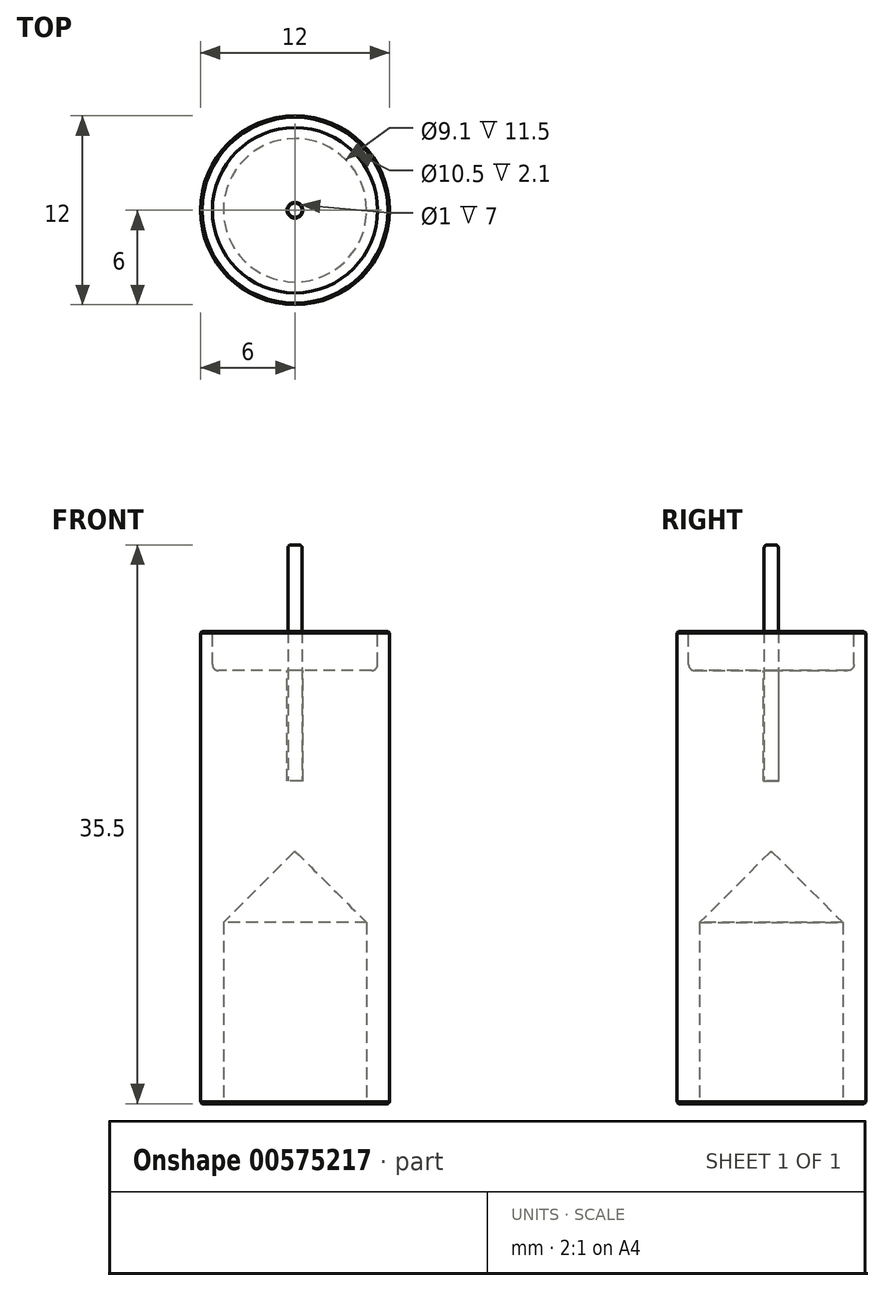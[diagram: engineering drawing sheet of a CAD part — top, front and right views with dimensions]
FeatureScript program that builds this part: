
annotation { "Feature Type Name" : "Feature", "Feature Type Description" : "" }
export const myFeature = defineFeature(function(context is Context, id is Id, definition is map)
    precondition{}
    {
        {
            var Q0;
            Q0=qCreatedBy(makeId("Top.planeOp"),FACE);
            var sketch = newSketch(context, id + "F0", { "sketchPlane" : qUnion([Q0])});
            skCircle(sketch, "E0", {"center": v(0, 0) * mm, "radius": 6 * mm});
            skSolve(sketch);
        }
        {
            var Q0;
            Q0 = qSketchRegion(id + "F0", true);
            extrude(context, id + "F1", {"entities" : qUnion([Q0]), "depth" : 30 * mm, "offsetDistance" : 25 * mm});
        }
        {
            var Q0;
            Q0=qCreatedBy(makeId("Top.planeOp"),FACE);
            var sketch = newSketch(context, id + "F2", { "sketchPlane" : qUnion([Q0])});
            skCircle(sketch, "E1", {"center": v(0, 0) * mm, "radius": 4.55 * mm});
            skSolve(sketch);
        }
        {
            var Q0;
            Q0 = qSketchRegion(id + "F2", true);
            extrude(context, id + "F3", {"entities" : qUnion([Q0]), "operationType" : NewBodyOperationType.REMOVE, "depth" : 16 * mm, "offsetDistance" : 25 * mm});
        }
        {
            var Q0;
            Q0=makeQuery(id+"F3.boolean.opBoolean","COPY",FACE,{"derivedFrom":makeQuery(id+"F3.opExtrude","CAP_FACE",FACE,{"disambiguationData":[OSD([sQuery(id+"F2.wireOp",EDGE,"E1")])],"isStart":false})});
            chamfer(context, id + "F4", {"entities" : qUnion([Q0]), "width" : 4.5 * mm, "tangentPropagation" : true});
        }
        {
            var Q0;
            Q0=makeQuery(id+"F1.opExtrude","CAP_FACE",FACE,{"disambiguationData":[OSD([sQuery(id+"F0.wireOp",EDGE,"E0")])],"isStart":false});
            var sketch = newSketch(context, id + "F5", { "sketchPlane" : qUnion([Q0])});
            skCircle(sketch, "E2", {"center": v(0, 0) * mm, "radius": 5.25 * mm});
            skSolve(sketch);
        }
        {
            var Q0;
            Q0 = qSketchRegion(id + "F5", true);
            extrude(context, id + "F6", {"entities" : qUnion([Q0]), "operationType" : NewBodyOperationType.REMOVE, "oppositeDirection" : true, "depth" : 2.5 * mm, "offsetDistance" : 25 * mm});
        }
        {
            var Q0;
            Q0=makeQuery(id+"F6.boolean.opBoolean","COPY",FACE,{"derivedFrom":makeQuery(id+"F6.opExtrude","CAP_FACE",FACE,{"disambiguationData":[OSD([sQuery(id+"F5.wireOp",EDGE,"E2")])],"isStart":false})});
            var sketch = newSketch(context, id + "F7", { "sketchPlane" : qUnion([Q0])});
            skCircle(sketch, "E3", {"center": v(0, 0) * mm, "radius": 0.5 * mm});
            skSolve(sketch);
        }
        {
            var Q0;
            Q0 = qSketchRegion(id + "F7", true);
            extrude(context, id + "F8", {"entities" : qUnion([Q0]), "operationType" : NewBodyOperationType.REMOVE, "oppositeDirection" : true, "depth" : 7 * mm, "offsetDistance" : 25 * mm});
        }
        {
            var Q0;
            Q0=makeQuery(id+"F1.opExtrude","CAP_EDGE",EDGE,{"disambiguationData":[OSD([sQuery(id+"F0.wireOp",EDGE,"E0")])],"isStart":false});
            var Q1;
            Q1=makeQuery(id+"F6.boolean.opBoolean","COPY",EDGE,{"derivedFrom":makeQuery(id+"F6.opExtrude","CAP_EDGE",EDGE,{"disambiguationData":[OSD([sQuery(id+"F5.wireOp",EDGE,"E2")])],"isStart":true})});
            var Q2;
            Q2=makeQuery(id+"F1.opExtrude","CAP_EDGE",EDGE,{"disambiguationData":[OSD([sQuery(id+"F0.wireOp",EDGE,"E0")])],"isStart":true});
            var Q3;
            Q3=makeQuery(id+"F3.boolean.opBoolean","COPY",EDGE,{"derivedFrom":makeQuery(id+"F3.opExtrude","CAP_EDGE",EDGE,{"disambiguationData":[OSD([sQuery(id+"F2.wireOp",EDGE,"E1")])],"isStart":true})});
            chamfer(context, id + "F9", {"entities" : qUnion([Q0, Q1, Q2, Q3]), "width" : .1 * mm, "tangentPropagation" : true});
        }
        {
            var Q0;
            Q0=makeQuery(id+"F6.boolean.opBoolean","COPY",EDGE,{"derivedFrom":makeQuery(id+"F6.opExtrude","CAP_EDGE",EDGE,{"disambiguationData":[OSD([sQuery(id+"F5.wireOp",EDGE,"E2")])],"isStart":false})});
            fillet(context, id + "F10", {"entities" : qUnion([Q0]), "radius" : .4 * mm, "tangentPropagation" : true, "allowEdgeOverflow" : false});
        }
        {
            var Q0;
            Q0=makeQuery(id+"F8.boolean.opBoolean","COPY",FACE,{"derivedFrom":makeQuery(id+"F8.opExtrude","CAP_FACE",FACE,{"disambiguationData":[OSD([sQuery(id+"F7.wireOp",EDGE,"E3")])],"isStart":false})});
            var sketch = newSketch(context, id + "F11", { "sketchPlane" : qUnion([Q0])});
            skCircle(sketch, "E4", {"center": v(0, 0) * mm, "radius": 0.45 * mm});
            skSolve(sketch);
        }
        {
            var Q0;
            Q0 = qSketchRegion(id + "F11", true);
            extrude(context, id + "F12", {"entities" : qUnion([Q0]), "operationType" : NewBodyOperationType.ADD, "depth" : 15 * mm, "offsetDistance" : 25 * mm});
        }
        {
            var Q0;
            Q0=makeQuery(id+"F12.opExtrude","CAP_EDGE",EDGE,{"disambiguationData":[OSD([sQuery(id+"F11.wireOp",EDGE,"E4")])],"isStart":false});
            fillet(context, id + "F13", {"entities" : qUnion([Q0]), "radius" : .2 * mm, "tangentPropagation" : true, "allowEdgeOverflow" : false});
        }
    });
